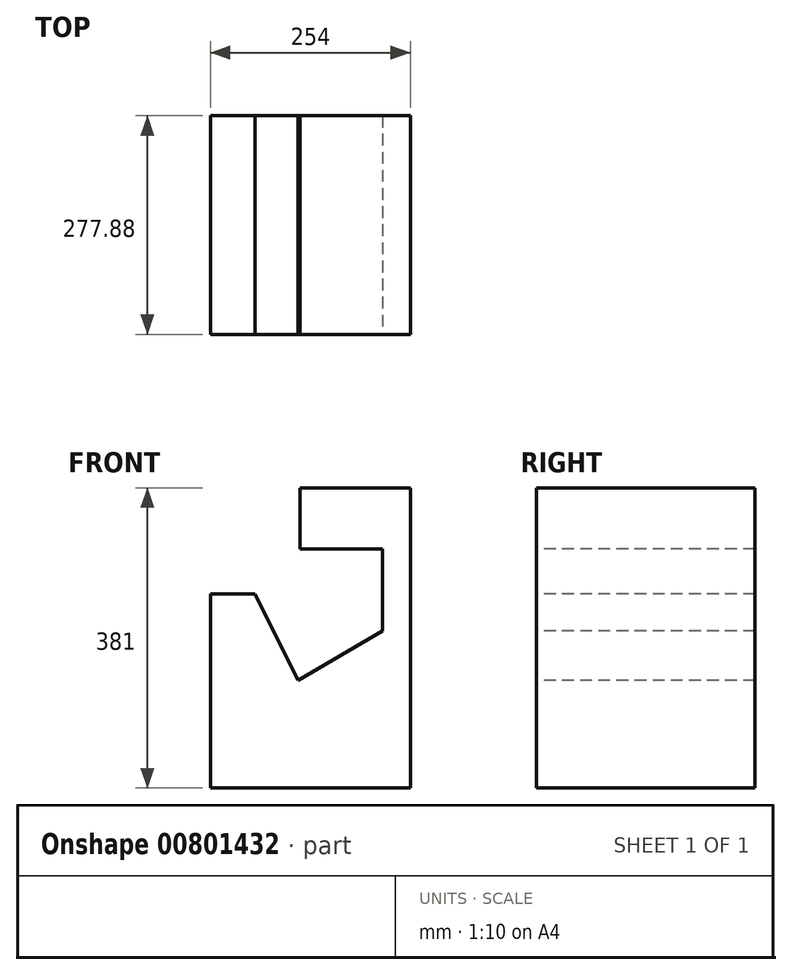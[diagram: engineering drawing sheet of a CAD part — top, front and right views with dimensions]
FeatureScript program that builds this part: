
annotation { "Feature Type Name" : "Feature", "Feature Type Description" : "" }
export const myFeature = defineFeature(function(context is Context, id is Id, definition is map)
    precondition{}
    {
        {
            var Q0;
            Q0=qCreatedBy(makeId("Front.planeOp"),FACE);
            var sketch = newSketch(context, id + "F0", { "sketchPlane" : qUnion([Q0])});
            skLineSegment(sketch, "E0.bottom", {"start": v(-138.08, 280.68) * mm, "end": v(115.92, 280.68) * mm});
            skLineSegment(sketch, "E0.top", {"start": v(-138.08, -100.32) * mm, "end": v(115.92, -100.32) * mm});
            skLineSegment(sketch, "E0.left", {"start": v(-138.08, 280.68) * mm, "end": v(-138.08, -100.32) * mm});
            skLineSegment(sketch, "E0.right", {"start": v(115.92, 280.68) * mm, "end": v(115.92, -100.32) * mm});
            skSolve(sketch);
        }
        {
            var Q0;
            Q0=makeQuery(id+"F0.imprint","IMPRINT",FACE,{"disambiguationData":[TD([[makeQuery(id+"F0.imprint","IMPRINT",EDGE,{"derivedFrom":sQuery(id+"F0.wireOp",EDGE,"E0.bottom")}),-1.0]])]});
            extrude(context, id + "F1", {"entities" : qUnion([Q0]), "depth" : 277.88 * mm, "offsetDistance" : 25.4 * mm});
        }
        {
            var Q0;
            Q0=makeQuery(id+"F1.opExtrude","CAP_FACE",FACE,{"disambiguationData":[OSD([sQuery(id+"F0.wireOp",EDGE,"E0.bottom"),sQuery(id+"F0.wireOp",EDGE,"E0.top"),sQuery(id+"F0.wireOp",EDGE,"E0.left"),sQuery(id+"F0.wireOp",EDGE,"E0.right")])],"isStart":false});
            var sketch = newSketch(context, id + "F2", { "sketchPlane" : qUnion([Q0])});
            skLineSegment(sketch, "E1.bottom", {"start": v(-138.08, 280.68) * mm, "end": v(-24.35, 280.68) * mm});
            skLineSegment(sketch, "E1.top", {"start": v(-138.08, 146.3) * mm, "end": v(-81.22, 146.3) * mm});
            skLineSegment(sketch, "E1.left", {"start": v(-138.08, 280.68) * mm, "end": v(-138.08, 146.3) * mm});
            skLineSegment(sketch, "E1.right", {"start": v(-24.35, 280.68) * mm, "end": v(-24.35, 202.83) * mm});
            skLineSegment(sketch, "E2", {"start": v(-81.22, 146.3) * mm, "end": v(-26.85, 36.03) * mm});
            skLineSegment(sketch, "E3", {"start": v(-26.85, 36.03) * mm, "end": v(80.27, 99.1) * mm});
            skLineSegment(sketch, "E4", {"start": v(80.27, 99.1) * mm, "end": v(80.27, 202.83) * mm});
            skLineSegment(sketch, "E5", {"start": v(80.27, 202.83) * mm, "end": v(-24.35, 202.83) * mm});
            skPoint(sketch, "E6.orphan", {"position": v(-24.35, 146.3) * mm});
            skSolve(sketch);
        }
        {
            var Q0;
            Q0=makeQuery(id+"F2.imprint","IMPRINT",FACE,{"disambiguationData":[TD([[makeQuery(id+"F2.imprint","IMPRINT",EDGE,{"derivedFrom":sQuery(id+"F2.wireOp",EDGE,"E1.bottom")}),-1.0]])]});
            extrude(context, id + "F3", {"entities" : qUnion([Q0]), "operationType" : NewBodyOperationType.REMOVE, "oppositeDirection" : true, "depth" : 496.82 * mm, "offsetDistance" : 25.4 * mm});
        }
    });
